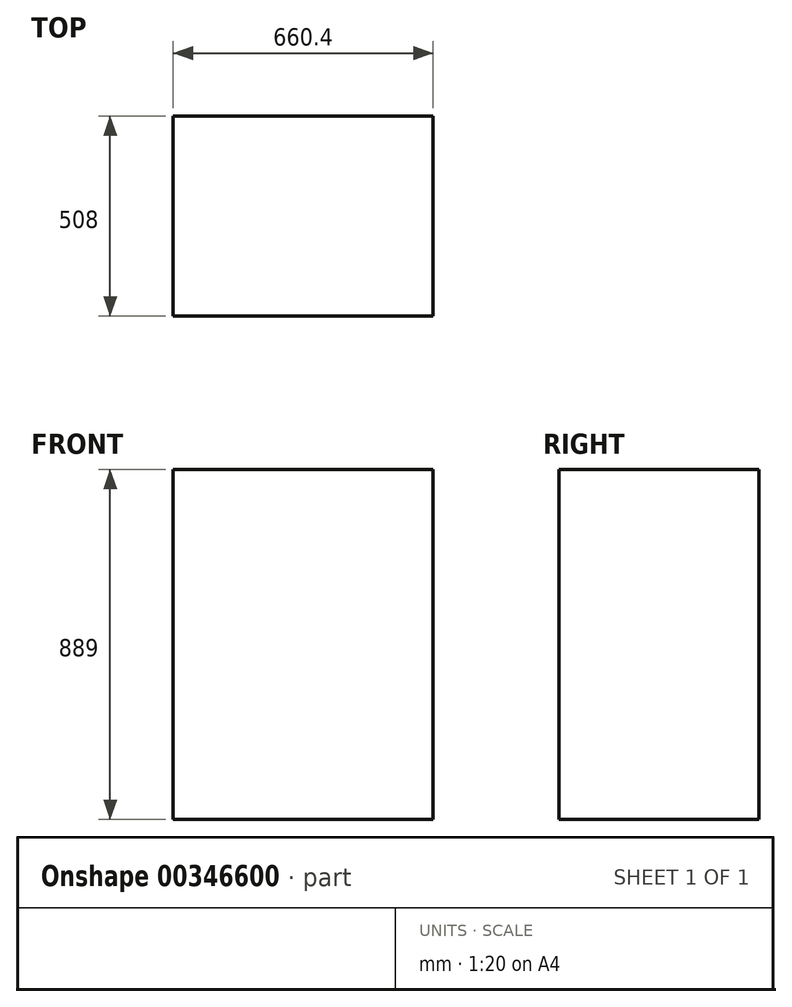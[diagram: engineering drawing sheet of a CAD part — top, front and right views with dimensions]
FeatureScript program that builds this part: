
annotation { "Feature Type Name" : "Feature", "Feature Type Description" : "" }
export const myFeature = defineFeature(function(context is Context, id is Id, definition is map)
    precondition{}
    {
        {
            var Q0;
            Q0=qCreatedBy(makeId("Top.planeOp"),FACE);
            var sketch = newSketch(context, id + "F0", { "sketchPlane" : qUnion([Q0])});
            skLineSegment(sketch, "E0.bottom", {"start": v(330.2, -254) * mm, "end": v(-330.2, -254) * mm});
            skLineSegment(sketch, "E0.top", {"start": v(330.2, 254) * mm, "end": v(-330.2, 254) * mm});
            skLineSegment(sketch, "E0.left", {"start": v(330.2, -254) * mm, "end": v(330.2, 254) * mm});
            skLineSegment(sketch, "E0.right", {"start": v(-330.2, -254) * mm, "end": v(-330.2, 254) * mm});
            skPoint(sketch, "E0.middle", {"position": v(0, 0) * mm});
            skSolve(sketch);
        }
        {
            var Q0;
            Q0=makeQuery(id+"F0.imprint","IMPRINT",FACE,{"disambiguationData":[TD([[makeQuery(id+"F0.imprint","IMPRINT",EDGE,{"derivedFrom":sQuery(id+"F0.wireOp",EDGE,"E0.bottom")}),-1.0]])]});
            extrude(context, id + "F1", {"entities" : qUnion([Q0]), "depth" : 889 * mm});
        }
    });
